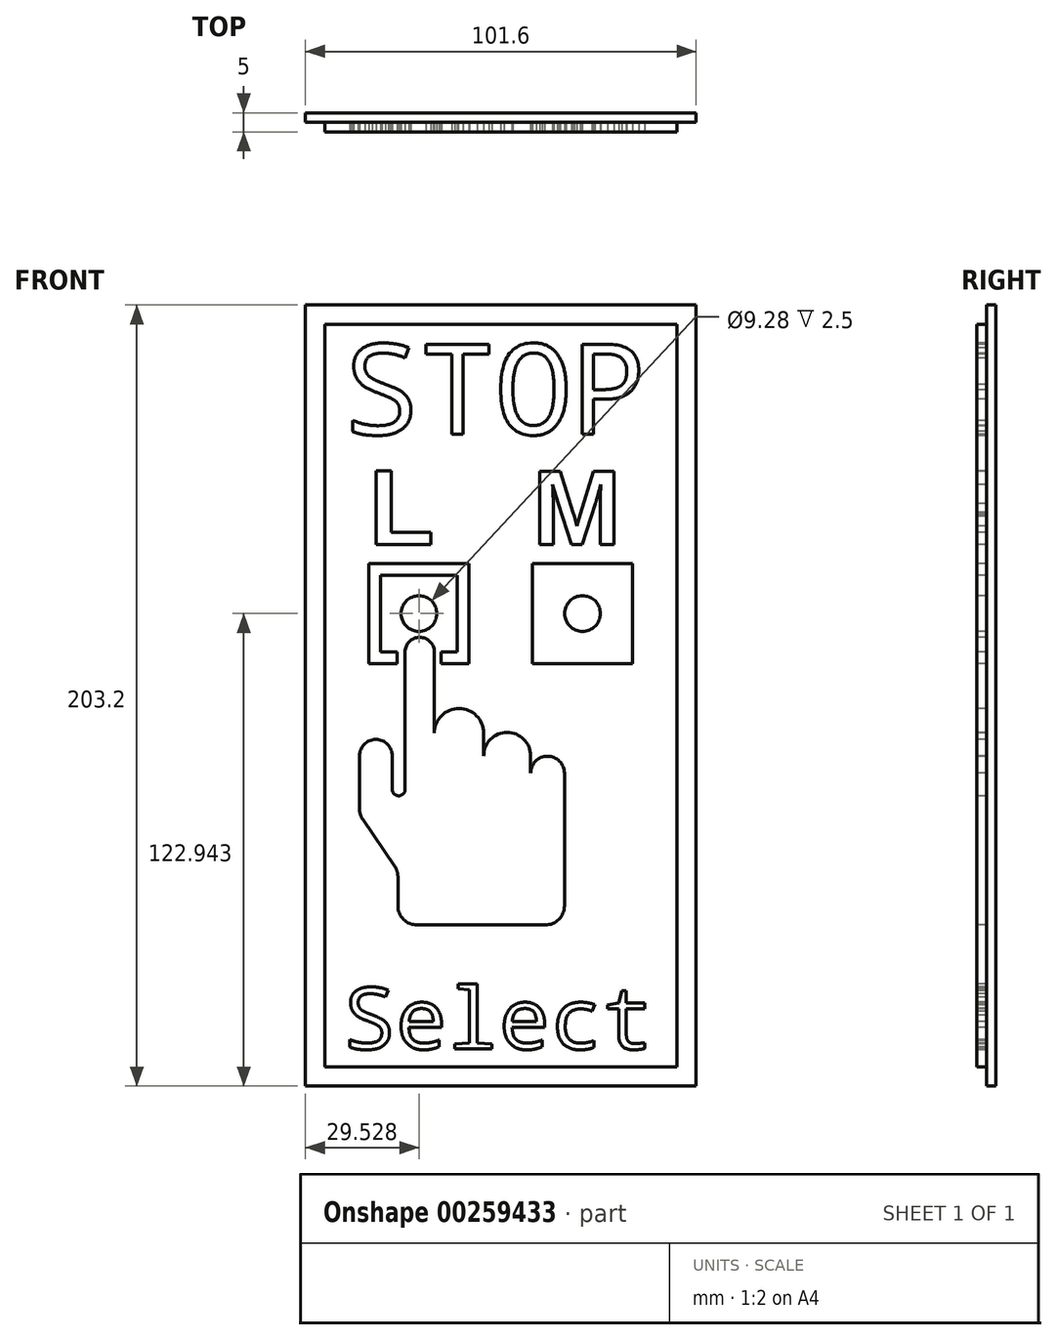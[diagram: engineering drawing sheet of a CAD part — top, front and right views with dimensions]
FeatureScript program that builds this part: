
annotation { "Feature Type Name" : "Feature", "Feature Type Description" : "" }
export const myFeature = defineFeature(function(context is Context, id is Id, definition is map)
    precondition{}
    {
        {
            var Q0;
            Q0=qCreatedBy(makeId("Front.planeOp"),FACE);
            var sketch = newSketch(context, id + "F0", { "sketchPlane" : qUnion([Q0])});
            skLineSegment(sketch, "E0.bottom", {"start": v(0, 0) * mm, "end": v(101.6, 0) * mm});
            skLineSegment(sketch, "E0.top", {"start": v(0, 203.2) * mm, "end": v(101.6, 203.2) * mm});
            skLineSegment(sketch, "E0.left", {"start": v(0, 0) * mm, "end": v(0, 203.2) * mm});
            skLineSegment(sketch, "E0.right", {"start": v(101.6, 0) * mm, "end": v(101.6, 203.2) * mm});
            skLineSegment(sketch, "E1.0", {"start": v(5, 5) * mm, "end": v(5, 198.2) * mm});
            skLineSegment(sketch, "E1.1", {"start": v(5, 5) * mm, "end": v(96.6, 5) * mm});
            skLineSegment(sketch, "E1.2", {"start": v(96.6, 5) * mm, "end": v(96.6, 198.2) * mm});
            skLineSegment(sketch, "E1.3", {"start": v(5, 198.2) * mm, "end": v(96.6, 198.2) * mm});
            skSolve(sketch);
        }
        {
            var Q0;
            Q0=makeQuery(id+"F0.imprint","IMPRINT",FACE,{"disambiguationData":[TD([[makeQuery(id+"F0.imprint","IMPRINT",EDGE,{"derivedFrom":sQuery(id+"F0.wireOp",EDGE,"E1.0")}),-1.0]])]});
            extrude(context, id + "F1", {"entities" : qUnion([Q0]), "depth" : 5 * mm, "offsetDistance" : 25 * mm});
        }
        {
            var Q0;
            Q0=makeQuery(id+"F0.imprint","IMPRINT",FACE,{"disambiguationData":[TD([[makeQuery(id+"F0.imprint","IMPRINT",EDGE,{"derivedFrom":sQuery(id+"F0.wireOp",EDGE,"E0.bottom")}),1.0]])]});
            extrude(context, id + "F2", {"entities" : qUnion([Q0]), "operationType" : NewBodyOperationType.ADD, "depth" : 2.5 * mm, "offsetDistance" : 25 * mm});
        }
        {
            var Q0;
            Q0=makeQuery(id+"F1.opExtrude","CAP_FACE",FACE,{"disambiguationData":[OSD([sQuery(id+"F0.wireOp",EDGE,"E1.0"),sQuery(id+"F0.wireOp",EDGE,"E1.1"),sQuery(id+"F0.wireOp",EDGE,"E1.2"),sQuery(id+"F0.wireOp",EDGE,"E1.3")])],"isStart":false});
            var sketch = newSketch(context, id + "F3", { "sketchPlane" : qUnion([Q0])});
            skLineSegment(sketch, "E2.0", {"start": v(10, 10) * mm, "end": v(10, 193.2) * mm, "construction": true});
            skLineSegment(sketch, "E2.1", {"start": v(10, 10) * mm, "end": v(91.6, 10) * mm, "construction": true});
            skLineSegment(sketch, "E2.2", {"start": v(91.6, 10) * mm, "end": v(91.6, 193.2) * mm, "construction": true});
            skLineSegment(sketch, "E2.3", {"start": v(10, 193.2) * mm, "end": v(91.6, 193.2) * mm, "construction": true});
            skText(sketch, "E3", { "text": "STOP", "fontName": "DroidSansMono.ttf"});
            skLineSegment(sketch, "E4.bottom", {"start": v(19.53, 132.94) * mm, "end": v(39.53, 132.94) * mm});
            skLineSegment(sketch, "E4.top", {"start": v(19.53, 112.94) * mm, "end": v(39.53, 112.94) * mm});
            skLineSegment(sketch, "E4.left", {"start": v(19.53, 132.94) * mm, "end": v(19.53, 112.94) * mm});
            skLineSegment(sketch, "E4.right", {"start": v(39.53, 132.94) * mm, "end": v(39.53, 112.94) * mm});
            skPoint(sketch, "E4.middle", {"position": v(29.53, 122.94) * mm});
            skLineSegment(sketch, "E5.0", {"start": v(16.53, 135.94) * mm, "end": v(42.53, 135.94) * mm});
            skLineSegment(sketch, "E5.1", {"start": v(16.53, 135.94) * mm, "end": v(16.53, 109.94) * mm});
            skLineSegment(sketch, "E5.2", {"start": v(16.53, 109.94) * mm, "end": v(42.53, 109.94) * mm});
            skLineSegment(sketch, "E5.3", {"start": v(42.53, 135.94) * mm, "end": v(42.53, 109.94) * mm});
            skCircle(sketch, "E6", {"center": v(29.53, 122.94) * mm, "radius": 4.64 * mm});
            skLineSegment(sketch, "E7", {"start": v(10, 116.25) * mm, "end": v(10, 95.36) * mm});
            skLineSegment(sketch, "E8", {"start": v(24.06, 54.43) * mm, "end": v(24.06, 46.92) * mm});
            skLineSegment(sketch, "E9", {"start": v(29.06, 41.92) * mm, "end": v(57.08, 41.92) * mm});
            skLineSegment(sketch, "E10", {"start": v(57.08, 41.92) * mm, "end": v(62.35, 41.92) * mm});
            skLineSegment(sketch, "E11", {"start": v(67.35, 46.92) * mm, "end": v(67.35, 81.44) * mm});
            skLineSegment(sketch, "E12", {"start": v(25.91, 112.94) * mm, "end": v(25.91, 77.18) * mm});
            skLineSegment(sketch, "E13", {"start": v(23.19, 57.25) * mm, "end": v(14.93, 69.34) * mm});
            skLineSegment(sketch, "E14", {"start": v(14.06, 72.16) * mm, "end": v(14.06, 85.93) * mm});
            skArc(sketch, "E15", {"start": v(22.59, 85.93) * mm, "mid": v(18.32, 90.2) * mm, "end": v(14.06, 85.93) * mm});
            skLineSegment(sketch, "E16", {"start": v(22.59, 85.93) * mm, "end": v(22.59, 77.18) * mm});
            skArc(sketch, "E17", {"start": v(22.59, 77.18) * mm, "mid": v(24.25, 75.52) * mm, "end": v(25.91, 77.18) * mm});
            skArc(sketch, "E18", {"start": v(33.53, 112.94) * mm, "mid": v(29.72, 116.75) * mm, "end": v(25.91, 112.94) * mm});
            skLineSegment(sketch, "E19", {"start": v(33.53, 112.94) * mm, "end": v(33.53, 91.84) * mm});
            skLineSegment(sketch, "E20", {"start": v(23.9, 112.94) * mm, "end": v(23.9, 109.94) * mm});
            skLineSegment(sketch, "E21", {"start": v(35.28, 112.94) * mm, "end": v(35.28, 109.94) * mm});
            skText(sketch, "E22", { "text": "Select", "fontName": "DroidSansMono.ttf"});
            skLineSegment(sketch, "E23", {"start": v(50.8, 169.55) * mm, "end": v(50.8, 115.43) * mm, "construction": true});
            skCircle(sketch, "E24.MirrorC", {"center": v(72.07, 122.94) * mm, "radius": 4.64 * mm});
            skLineSegment(sketch, "E25.MirrorCS", {"start": v(59.07, 135.94) * mm, "end": v(59.07, 109.94) * mm});
            skLineSegment(sketch, "E26.MirrorCS", {"start": v(85.07, 109.94) * mm, "end": v(59.07, 109.94) * mm});
            skLineSegment(sketch, "E27.MirrorCS", {"start": v(85.07, 135.94) * mm, "end": v(85.07, 109.94) * mm});
            skLineSegment(sketch, "E28.MirrorCS", {"start": v(85.07, 135.94) * mm, "end": v(59.07, 135.94) * mm});
            skLineSegment(sketch, "E29.MirrorCS", {"start": v(62.07, 132.94) * mm, "end": v(62.07, 112.94) * mm});
            skLineSegment(sketch, "E30.MirrorCS", {"start": v(82.07, 132.94) * mm, "end": v(82.07, 112.94) * mm});
            skLineSegment(sketch, "E31.MirrorCS", {"start": v(82.07, 112.94) * mm, "end": v(62.07, 112.94) * mm});
            skLineSegment(sketch, "E32.MirrorCS", {"start": v(82.07, 132.94) * mm, "end": v(62.07, 132.94) * mm});
            skLineSegment(sketch, "E33.0", {"start": v(16.53, 140.94) * mm, "end": v(42.53, 140.94) * mm, "construction": true});
            skLineSegment(sketch, "E34.MirrorCS", {"start": v(85.07, 140.94) * mm, "end": v(59.07, 140.94) * mm, "construction": true});
            skText(sketch, "E35", { "text": "L", "fontName": "Arimo-Bold.ttf"});
            skText(sketch, "E36", { "text": "M", "fontName": "Arimo-Bold.ttf"});
            skPoint(sketch, "E37.visualSharp", {"position": v(14.06, 70.62) * mm});
            skArc(sketch, "E37.filletArc", {"start": v(14.06, 72.16) * mm, "mid": v(14.28, 70.69) * mm, "end": v(14.93, 69.34) * mm});
            skPoint(sketch, "E38.visualSharp", {"position": v(24.06, 55.98) * mm});
            skArc(sketch, "E38.filletArc", {"start": v(24.06, 54.43) * mm, "mid": v(23.84, 55.9) * mm, "end": v(23.19, 57.25) * mm});
            skPoint(sketch, "E39.visualSharp", {"position": v(24.06, 41.92) * mm});
            skArc(sketch, "E39.filletArc", {"start": v(24.06, 46.92) * mm, "mid": v(25.52, 43.39) * mm, "end": v(29.06, 41.92) * mm});
            skPoint(sketch, "E40.visualSharp", {"position": v(67.35, 41.92) * mm});
            skArc(sketch, "E40.filletArc", {"start": v(62.35, 41.92) * mm, "mid": v(65.89, 43.39) * mm, "end": v(67.35, 46.92) * mm});
            skArc(sketch, "E41", {"start": v(46.37, 91.84) * mm, "mid": v(39.95, 98.25) * mm, "end": v(33.53, 91.84) * mm});
            skLineSegment(sketch, "E42", {"start": v(46.37, 91.84) * mm, "end": v(46.37, 85.93) * mm});
            skArc(sketch, "E43", {"start": v(58.56, 85.93) * mm, "mid": v(52.46, 92.03) * mm, "end": v(46.37, 85.93) * mm});
            skLineSegment(sketch, "E44", {"start": v(58.56, 85.93) * mm, "end": v(58.56, 81.44) * mm});
            skArc(sketch, "E45", {"start": v(67.35, 81.44) * mm, "mid": v(62.96, 85.83) * mm, "end": v(58.56, 81.44) * mm});
            const initialGuessF3  = {"E3": [0.01, 0.16955, 1, 0, 0.02365], "E22": [0.01, 0.00965, 1, 0, 0.01609], "E35": [0.01653, 0.14094, 1, 0, 0.01996], "E36": [0.05907, 0.14094, 1, 0, 0.01986]};
            skSetInitialGuess(sketch, initialGuessF3);
            skSolve(sketch);
        }
        {
            var Q0;
            Q0=makeQuery(id+"F3.imprint","IMPRINT",FACE,{"disambiguationData":[TD([[makeQuery(id+"F3.imprint","IMPRINT",EDGE,{"derivedFrom":sQuery(id+"F3.wireOp",EDGE,"E3.sketch_text.stroke-0")}),-1.0]])]});
            var Q1;
            Q1=makeQuery(id+"F3.imprint","IMPRINT",FACE,{"disambiguationData":[TD([[makeQuery(id+"F3.imprint","IMPRINT",EDGE,{"derivedFrom":sQuery(id+"F3.wireOp",EDGE,"E3.sketch_text.stroke-20")}),-1.0]])]});
            var Q2;
            Q2=makeQuery(id+"F3.imprint","IMPRINT",FACE,{"disambiguationData":[TD([[makeQuery(id+"F3.imprint","IMPRINT",EDGE,{"derivedFrom":sQuery(id+"F3.wireOp",EDGE,"E22.sketch_text.stroke-0")}),-1.0]])]});
            var Q3;
            Q3=makeQuery(id+"F3.imprint","IMPRINT",FACE,{"disambiguationData":[TD([[makeQuery(id+"F3.imprint","IMPRINT",EDGE,{"derivedFrom":sQuery(id+"F3.wireOp",EDGE,"E22.sketch_text.stroke-35")}),-1.0]])]});
            var Q4;
            Q4=makeQuery(id+"F3.imprint","IMPRINT",FACE,{"disambiguationData":[TD([[makeQuery(id+"F3.imprint","IMPRINT",EDGE,{"derivedFrom":sQuery(id+"F3.wireOp",EDGE,"E22.sketch_text.stroke-60")}),-1.0]])]});
            var Q5;
            Q5=makeQuery(id+"F3.imprint","IMPRINT",FACE,{"disambiguationData":[TD([[makeQuery(id+"F3.imprint","IMPRINT",EDGE,{"derivedFrom":sQuery(id+"F3.wireOp",EDGE,"E22.sketch_text.stroke-72")}),-1.0]])]});
            var Q6;
            Q6=makeQuery(id+"F3.imprint","IMPRINT",FACE,{"disambiguationData":[TD([[makeQuery(id+"F3.imprint","IMPRINT",EDGE,{"derivedFrom":sQuery(id+"F3.wireOp",EDGE,"E3.sketch_text.stroke-28")}),-1.0]])]});
            var Q7;
            Q7=makeQuery(id+"F3.imprint","IMPRINT",FACE,{"disambiguationData":[TD([[makeQuery(id+"F3.imprint","IMPRINT",EDGE,{"derivedFrom":sQuery(id+"F3.wireOp",EDGE,"E3.sketch_text.stroke-40")}),-1.0]])]});
            var Q8;
            Q8=makeQuery(id+"F3.imprint","IMPRINT",FACE,{"disambiguationData":[TD([[makeQuery(id+"F3.imprint","IMPRINT",EDGE,{"derivedFrom":sQuery(id+"F3.wireOp",EDGE,"E8")}),1.0]])]});
            var Q9;
            Q9=makeQuery(id+"F3.imprint","IMPRINT",FACE,{"disambiguationData":[TD([[makeQuery(id+"F3.imprint","IMPRINT",EDGE,{"derivedFrom":sQuery(id+"F3.wireOp",EDGE,"E22.sketch_text.stroke-20")}),-1.0]])]});
            var Q10;
            Q10=makeQuery(id+"F3.imprint","IMPRINT",FACE,{"disambiguationData":[TD([[makeQuery(id+"F3.imprint","IMPRINT",EDGE,{"derivedFrom":sQuery(id+"F3.wireOp",EDGE,"E22.sketch_text.stroke-45")}),-1.0]])]});
            var Q11;
            Q11=makeQuery(id+"F3.imprint","IMPRINT",FACE,{"disambiguationData":[TD([[makeQuery(id+"F3.imprint","IMPRINT",EDGE,{"derivedFrom":sQuery(id+"F3.wireOp",EDGE,"E4.bottom")}),1.0]])]});
            var Q12;
            {var subQ1=sQuery(id+"F3.wireOp",EDGE,"E12");var subQ6=sQuery(id+"F3.wireOp",EDGE,"E5.2");var subQ7=makeQuery(id+"F3.imprint","INTERSECT",VERTEX,{"derivedFrom":[subQ6,subQ1]});Q12=makeQuery(id+"F3.imprint","IMPRINT",FACE,{"disambiguationData":[TD([[makeQuery(id+"F3.imprint","IMPRINT",EDGE,{"disambiguationData":[TD([[subQ7,-1.0]])],"derivedFrom":subQ6}),1.0]])]});}
            var Q13;
            Q13=makeQuery(id+"F3.imprint","IMPRINT",FACE,{"disambiguationData":[TD([[makeQuery(id+"F3.imprint","IMPRINT",EDGE,{"derivedFrom":sQuery(id+"F3.wireOp",EDGE,"E6")}),1.0]])]});
            var Q14;
            {var subQ0=sQuery(id+"F3.wireOp",EDGE,"E18");Q14=makeQuery(id+"F3.imprint","IMPRINT",FACE,{"disambiguationData":[TD([[makeQuery(id+"F3.imprint","IMPRINT",EDGE,{"derivedFrom":subQ0}),1.0]])]});}
            var Q15;
            Q15=makeQuery(id+"F3.imprint","IMPRINT",FACE,{"disambiguationData":[TD([[makeQuery(id+"F3.imprint","IMPRINT",EDGE,{"derivedFrom":sQuery(id+"F3.wireOp",EDGE,"E25.MirrorCS")}),1.0]])]});
            var Q16;
            Q16=makeQuery(id+"F3.imprint","IMPRINT",FACE,{"disambiguationData":[TD([[makeQuery(id+"F3.imprint","IMPRINT",EDGE,{"derivedFrom":sQuery(id+"F3.wireOp",EDGE,"E24.MirrorC")}),-1.0]])]});
            var Q17;
            Q17=makeQuery(id+"F3.imprint","IMPRINT",FACE,{"disambiguationData":[TD([[makeQuery(id+"F3.imprint","IMPRINT",EDGE,{"derivedFrom":sQuery(id+"F3.wireOp",EDGE,"E35.sketch_text.stroke-0")}),-1.0]])]});
            var Q18;
            Q18=makeQuery(id+"F3.imprint","IMPRINT",FACE,{"disambiguationData":[TD([[makeQuery(id+"F3.imprint","IMPRINT",EDGE,{"derivedFrom":sQuery(id+"F3.wireOp",EDGE,"E36.sketch_text.stroke-0")}),-1.0]])]});
            extrude(context, id + "F4", {"entities" : qUnion([Q0, Q1, Q2, Q3, Q4, Q5, Q6, Q7, Q8, Q9, Q10, Q11, Q12, Q13, Q14, Q15, Q16, Q17, Q18]), "operationType" : NewBodyOperationType.REMOVE, "oppositeDirection" : true, "depth" : 2.5 * mm, "offsetDistance" : 25 * mm});
        }
    });
